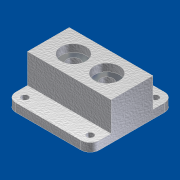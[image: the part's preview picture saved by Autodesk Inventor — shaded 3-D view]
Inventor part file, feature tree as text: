
AUTODESK INVENTOR PART (.ipt)
format: ipt  version: unknown  size: 245,248 bytes
history: native  units: mm
features: sketch x6, extrude x4, hole x2, fillet x1
ambient origin geometry x8: Origin, YZ Plane, XZ Plane, XY Plane, X Axis, Y Axis, Z Axis, Center Point
feature tree (13):
  extrude  "Extrusion1"  Depth=22.5mm TaperAngle=0.0deg
  fillet  "Fillet1"  Radius=5.5mm
  extrude  "Extrusion2"  Depth=5.0mm TaperAngle=0.0deg
  extrude  "Extrusion4"  Depth=17.5mm TaperAngle=0.0deg
  extrude  "Extrusion5"  Depth=16.0mm
  hole  "Hole1"  [1 undecoded]
  hole  "Hole2"  [1 undecoded]
  sketch  "Sketch1"  dims[d0=50.0mm d1=22.5mm d2=0.0mm d3=5.5mm]
  sketch  "Sketch2"  dims[d4=40.0mm d5=5.0mm d6=0.0mm]
  sketch  "Sketch4"  dims[d10=25.0mm d11=17.5mm d12=0.0mm]
  sketch  "Sketch5"  dims[d13=36.0mm d14=16.0mm]
  sketch  "Sketch6"  dims[d15=17.5mm d16=0.0mm d17=20.0mm]
  sketch  "Sketch7"  dims[d18=7.5mm d19=6.0mm d20=15.0mm d21=4.5mm d22=90.0deg d23=8.0mm d24=20.594885mm d25=4.0mm d26=6.0mm d27=15.0mm d28=4.5mm d29=90.0deg d30=8.0mm d31=20.594885mm]
note: 2 required parameter values undecoded (feature->parameter linkage not recoverable at this tier; creation-order binding heuristic only, values carry confidence <= 0.55)
